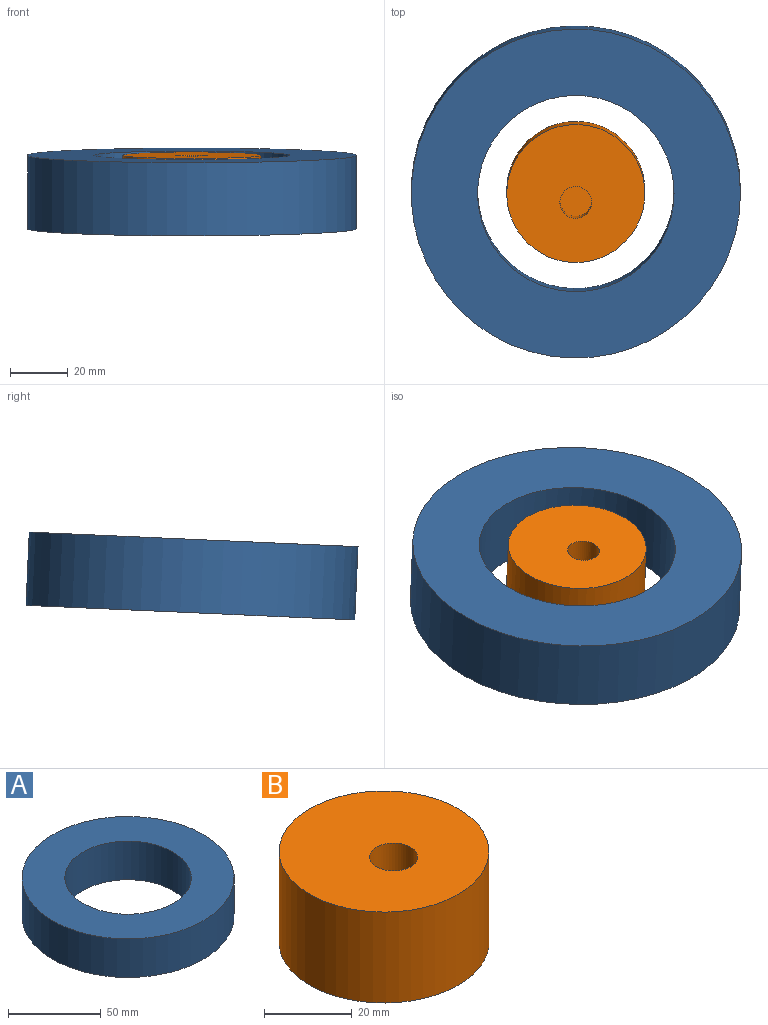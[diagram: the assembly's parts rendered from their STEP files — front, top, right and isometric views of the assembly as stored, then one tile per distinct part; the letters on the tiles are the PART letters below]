
ASSEMBLY  parts=2 mates=1
PART A: 4 faces, bbox 114.1x114.1x25.4 mm
  f0: cylinder r=34.04mm len=68.09mm, axis (0,0,-1), area 5433.3mm2, adj f2,f3
  f1: cylinder r=57.07mm len=114.14mm, axis (0,0,-1), area 9107.8mm2, adj f2,f3
  f2: plane 114.14x114.14mm, normal (0,0,1), area 6590.5mm2, adj f0,f1
  f3: plane 114.14x114.14mm, normal (0,0,-1), area 6590.5mm2, adj f0,f1
PART B: 5 faces, bbox 47.9x47.9x25.4 mm
  f0: cylinder r=23.94mm len=47.88mm, axis (0,0,-1), area 3820.7mm2, adj f1,f2
  f1: plane 47.88x47.88mm, normal (0,0,1), area 1705.3mm2, adj f0,f3
  f2: plane 47.88x47.88mm, normal (0,0,-1), area 1800.6mm2, adj f0
  f3: cylinder r=5.51mm len=15.44mm, axis (0,0,1), area 534.4mm2, adj f1,f4
  f4: plane 11.01x11.01mm, normal (0,0,1), area 95.3mm2, adj f3
PLACE A rot(axis=(1,0,0),2.5deg) t=(-66.34,-39.21,17.75)mm
PLACE B rot(axis=(1,0,0),2.5deg) t=(50.82,37.47,21.15)mm
MATE fastened A.f0 <-> B.f0  axis (0,0.04,-1) through (50.82,36.91,33.84)mm
